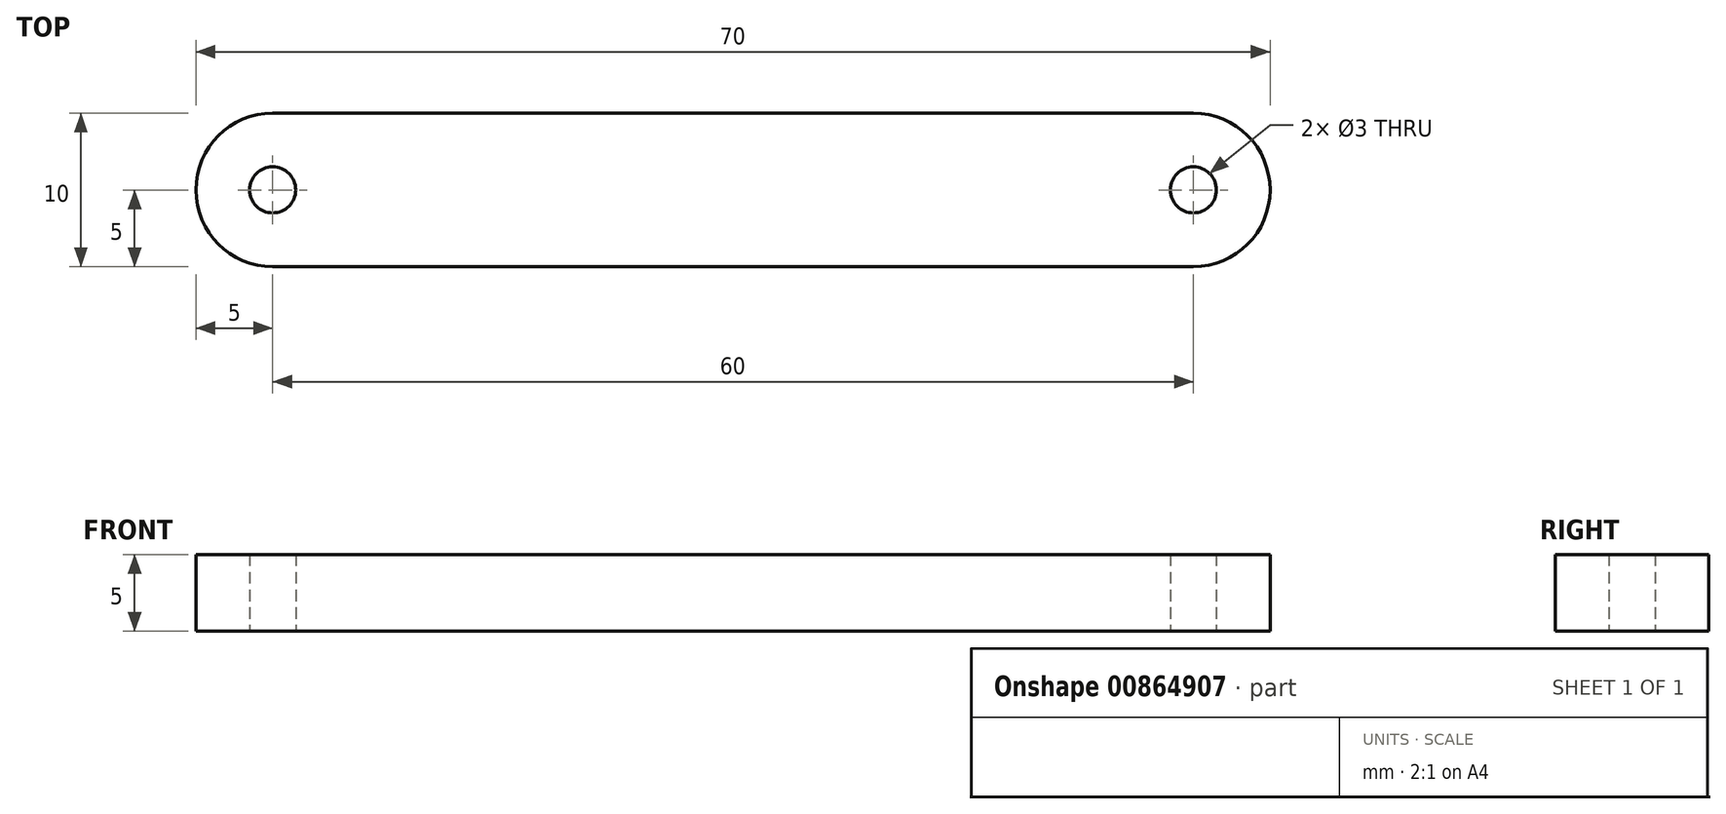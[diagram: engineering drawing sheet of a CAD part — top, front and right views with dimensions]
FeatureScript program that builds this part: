
annotation { "Feature Type Name" : "Feature", "Feature Type Description" : "" }
export const myFeature = defineFeature(function(context is Context, id is Id, definition is map)
    precondition{}
    {
        {
            var Q0;
            Q0=qCreatedBy(makeId("Top.planeOp"),FACE);
            var sketch = newSketch(context, id + "F0", { "sketchPlane" : qUnion([Q0])});
            skArc(sketch, "E0", {"start": v(0, 5) * mm, "mid": v(-5, 0) * mm, "end": v(0, -5) * mm});
            skLineSegment(sketch, "E1", {"start": v(0, 0) * mm, "end": v(60, 0) * mm, "construction": true});
            skArc(sketch, "E2", {"start": v(60, -5) * mm, "mid": v(65, 0) * mm, "end": v(60, 5) * mm});
            skLineSegment(sketch, "E3", {"start": v(0, -5) * mm, "end": v(60, -5) * mm});
            skLineSegment(sketch, "E4", {"start": v(0, 5) * mm, "end": v(60, 5) * mm});
            skCircle(sketch, "E5", {"center": v(0, 0) * mm, "radius": 1.5 * mm});
            skCircle(sketch, "E6", {"center": v(60, 0) * mm, "radius": 1.5 * mm});
            skSolve(sketch);
        }
        {
            var Q0;
            Q0=makeQuery(id+"F0.imprint","IMPRINT",FACE,{"disambiguationData":[TD([[makeQuery(id+"F0.imprint","IMPRINT",EDGE,{"derivedFrom":sQuery(id+"F0.wireOp",EDGE,"E0")}),1.0]])]});
            extrude(context, id + "F1", {"entities" : qUnion([Q0]), "depth" : 5 * mm, "offsetDistance" : 25 * mm});
        }
    });
